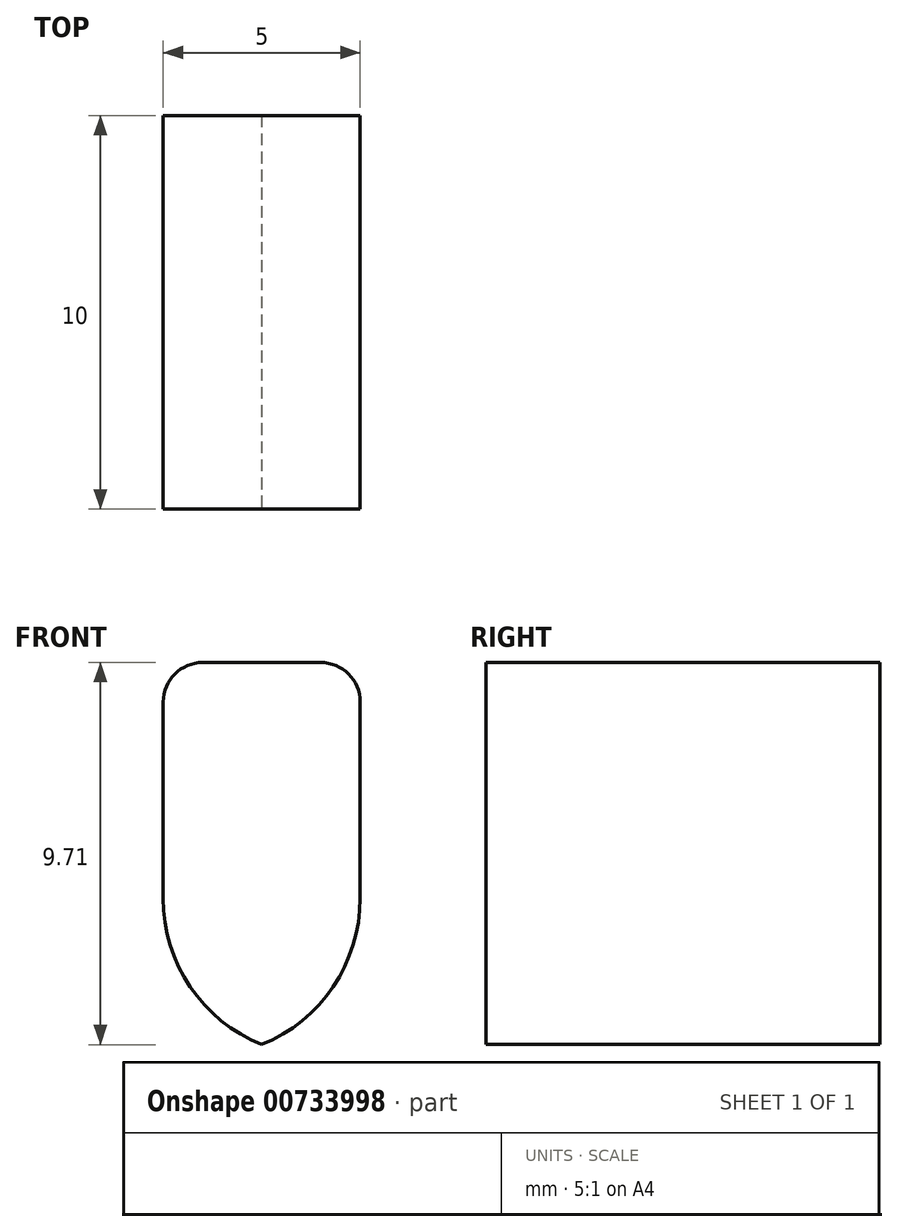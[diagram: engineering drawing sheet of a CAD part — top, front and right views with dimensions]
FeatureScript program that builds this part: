
annotation { "Feature Type Name" : "Feature", "Feature Type Description" : "" }
export const myFeature = defineFeature(function(context is Context, id is Id, definition is map)
    precondition{}
    {
        {
            var Q0;
            Q0=qCreatedBy(makeId("Front.planeOp"),FACE);
            var sketch = newSketch(context, id + "F0", { "sketchPlane" : qUnion([Q0])});
            skLineSegment(sketch, "E0.bottom", {"start": v(-79.75, -79.75) * mm, "end": v(79.75, -79.75) * mm});
            skLineSegment(sketch, "E0.top", {"start": v(-79.75, 79.75) * mm, "end": v(79.75, 79.75) * mm});
            skLineSegment(sketch, "E0.left", {"start": v(-79.75, -79.75) * mm, "end": v(-79.75, 79.75) * mm});
            skLineSegment(sketch, "E0.right", {"start": v(79.75, -79.75) * mm, "end": v(79.75, 79.75) * mm});
            skPoint(sketch, "E0.middle", {"position": v(0, 0) * mm});
            skCircle(sketch, "E1", {"center": v(0, 0) * mm, "radius": 60.75 * mm});
            skLineSegment(sketch, "E2", {"start": v(0, 0) * mm, "end": v(0, -60) * mm});
            skCircle(sketch, "E3", {"center": v(-60, -60) * mm, "radius": 5.05 * mm});
            skCircle(sketch, "E4", {"center": v(60, -60) * mm, "radius": 5.05 * mm});
            skPoint(sketch, "E5.top.start.orphan", {"position": v(-1.76, -101.34) * mm});
            skPoint(sketch, "E6.trimOffspring.end.orphan", {"position": v(3.24, -101.34) * mm});
            skPoint(sketch, "E7.orphan", {"position": v(-3.24, 101.34) * mm});
            skPoint(sketch, "E8.orphan", {"position": v(1.76, 101.34) * mm});
            skLineSegment(sketch, "E9", {"start": v(-60, -60) * mm, "end": v(60, -60) * mm});
            skLineSegment(sketch, "E10", {"start": v(0, 0) * mm, "end": v(2.5, 0) * mm});
            skLineSegment(sketch, "E11", {"start": v(2.5, 0) * mm, "end": v(2.5, 79.75) * mm});
            skLineSegment(sketch, "E12", {"start": v(2.5, 79.75) * mm, "end": v(2.5, -79.75) * mm});
            skLineSegment(sketch, "E13", {"start": v(2.5, -79.75) * mm, "end": v(-2.5, -79.75) * mm});
            skLineSegment(sketch, "E14", {"start": v(-2.5, -79.75) * mm, "end": v(-2.5, 79.75) * mm});
            skLineSegment(sketch, "E15", {"start": v(0, -79.75) * mm, "end": v(0, -69.75) * mm});
            skLineSegment(sketch, "E16", {"start": v(0, -69.75) * mm, "end": v(-2.5, -69.75) * mm});
            skLineSegment(sketch, "E17", {"start": v(-2.5, -69.75) * mm, "end": v(2.5, -69.75) * mm});
            skSolve(sketch);
        }
        {
            var Q0;
            {var subQ0=sQuery(id+"F0.wireOp",EDGE,"E5.left");Q0=makeQuery(id+"F0.imprint","IMPRINT",FACE,{"disambiguationData":[TD([[makeQuery(id+"F0.imprint","IMPRINT",EDGE,{"derivedFrom":subQ0}),-1.0]])]});}
            var Q1;
            {var subQ5=sQuery(id+"F0.wireOp",EDGE,"E5.right");Q1=makeQuery(id+"F0.imprint","IMPRINT",FACE,{"disambiguationData":[TD([[makeQuery(id+"F0.imprint","IMPRINT",EDGE,{"derivedFrom":subQ5}),1.0]])]});}
            var Q2;
            {var subQ6=sQuery(id+"F0.wireOp",EDGE,"E0.bottom");Q2=makeQuery(id+"F0.imprint","IMPRINT",FACE,{"disambiguationData":[TD([[makeQuery(id+"F0.imprint","IMPRINT",EDGE,{"derivedFrom":subQ6}),1.0]])]});}
            var Q3;
            {var subQ3=sQuery(id+"F0.wireOp",EDGE,"E15");Q3=makeQuery(id+"F0.imprint","IMPRINT",FACE,{"disambiguationData":[TD([[makeQuery(id+"F0.imprint","IMPRINT",EDGE,{"derivedFrom":subQ3}),1.0]])]});}
            var Q4;
            {var subQ5=sQuery(id+"F0.wireOp",EDGE,"E15");Q4=makeQuery(id+"F0.imprint","IMPRINT",FACE,{"disambiguationData":[TD([[makeQuery(id+"F0.imprint","IMPRINT",EDGE,{"derivedFrom":subQ5}),-1.0]])]});}
            extrude(context, id + "F1", {"entities" : qUnion([Q0, Q1, Q2, Q3, Q4]), "depth" : 10 * mm, "offsetDistance" : 25 * mm});
        }
        {
            var Q0;
            Q0=makeQuery(id+"F1.opExtrude","SWEPT_EDGE",EDGE,{"disambiguationData":[OSD([sQuery(id+"F0.wireOp",EDGE,"E0.top"),sQuery(id+"F0.wireOp",EDGE,"E0.right")])]});
            var Q1;
            Q1=makeQuery(id+"F1.opExtrude","SWEPT_EDGE",EDGE,{"disambiguationData":[OSD([sQuery(id+"F0.wireOp",EDGE,"E0.top"),sQuery(id+"F0.wireOp",EDGE,"E0.left")])]});
            var Q2;
            Q2=makeQuery(id+"F1.opExtrude","SWEPT_EDGE",EDGE,{"disambiguationData":[OSD([sQuery(id+"F0.wireOp",EDGE,"E0.top"),sQuery(id+"F0.wireOp",EDGE,"E5.left")])]});
            var Q3;
            Q3=makeQuery(id+"F1.opExtrude","SWEPT_EDGE",EDGE,{"disambiguationData":[OSD([sQuery(id+"F0.wireOp",EDGE,"E0.top"),sQuery(id+"F0.wireOp",EDGE,"E5.right")])]});
            var Q4;
            Q4=makeQuery(id+"F1.opExtrude","SWEPT_EDGE",EDGE,{"disambiguationData":[OSD([sQuery(id+"F0.wireOp",EDGE,"E0.bottom"),sQuery(id+"F0.wireOp",EDGE,"E0.left")])]});
            var Q5;
            Q5=makeQuery(id+"F1.opExtrude","SWEPT_EDGE",EDGE,{"disambiguationData":[OSD([sQuery(id+"F0.wireOp",EDGE,"E0.bottom"),sQuery(id+"F0.wireOp",EDGE,"E0.right")])]});
            var Q6;
            Q6=makeQuery(id+"F1.opExtrude","SWEPT_EDGE",EDGE,{"disambiguationData":[OSD([sQuery(id+"F0.wireOp",EDGE,"E1"),sQuery(id+"F0.wireOp",EDGE,"E5.left")])]});
            var Q7;
            Q7=makeQuery(id+"F1.opExtrude","SWEPT_EDGE",EDGE,{"disambiguationData":[OSD([sQuery(id+"F0.wireOp",EDGE,"E1"),sQuery(id+"F0.wireOp",EDGE,"E5.right")])]});
            fillet(context, id + "F2", {"entities" : qUnion([Q0, Q1, Q2, Q3, Q4, Q5, Q6, Q7]), "radius" : 4 * mm, "tangentPropagation" : true, "allowEdgeOverflow" : false});
        }
        {
            var Q0;
            Q0=makeQuery(id+"F1.opExtrude","SWEPT_EDGE",EDGE,{"disambiguationData":[OSD([sQuery(id+"F0.wireOp",EDGE,"E14"),sQuery(id+"F0.wireOp",EDGE,"E17")])]});
            var Q1;
            Q1=makeQuery(id+"F1.opExtrude","SWEPT_EDGE",EDGE,{"disambiguationData":[OSD([sQuery(id+"F0.wireOp",EDGE,"E12"),sQuery(id+"F0.wireOp",EDGE,"E17")])]});
            fillet(context, id + "F3", {"entities" : qUnion([Q0, Q1]), "radius" : 1 * mm, "tangentPropagation" : true, "allowEdgeOverflow" : false});
        }
    });
